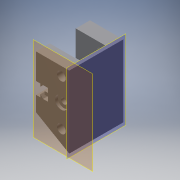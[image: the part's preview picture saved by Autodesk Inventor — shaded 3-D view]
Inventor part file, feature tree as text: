
AUTODESK INVENTOR PART (.ipt)
format: ipt  version: 2016 (Build 200138000, 138)  size: 259,584 bytes
history: native  units: in
note: dims shown in document units (in); Inventor stores cm internally (conversion verified against a paired STEP export)
features: sketch x10, extrude x10, projected_geometry x8, plane x4, reference x1
ambient origin geometry x8: Origin, YZ Plane, XZ Plane, XY Plane, X Axis, Y Axis, Z Axis, Center Point
bodies: Solid1 (feature_tree)
feature tree (33):
  plane  "Work Plane1"
  plane  "Work Plane2"
  sketch  "Sketch1"  dims[d0=60.0deg d1=1.0in d2=0.0in]
  plane  "Work Plane3"
  extrude  "Extrusion1"  Depth=1.0in TaperAngle=0.0deg
  extrude  "Extrusion2"  Depth=0.6299in
  extrude  "Extrusion3"  Depth=0.4331in
  extrude  "Extrusion4"  Depth=0.9055in
  sketch  "Sketch5"  dims[d11=0.1969in d12=0.0in d13=0.5in]
  plane  "Work Plane4"
  extrude  "Extrusion5"  Depth=0.5in
  extrude  "Extrusion6"  Depth=0.2756in TaperAngle=0.0deg
  extrude  "Extrusion7"  Depth=0.8661in
  extrude  "Extrusion8"  Depth=0.1181in
  extrude  "Extrusion9"  Depth=0.2362in
  extrude  "Extrusion10"  Depth=0.1969in
  reference  "Reference1"
  sketch  "Sketch2"  dims[d3=2.4375in d4=0.0in d5=0.6299in]
  sketch  "Sketch3"  dims[d6=0.6299in d7=0.4331in]
  projected_geometry  "Projected Loop1"
  sketch  "Sketch4"  dims[d8=8.9375in d9=0.0in d10=0.9055in]
  projected_geometry  "Projected Loop2"
  sketch  "Sketch6"  dims[d14=0.1969in d15=0.0in d16=0.2756in d17=0.0in]
  projected_geometry  "Projected Loop3"
  sketch  "Sketch7"  dims[d18=0.8661in d19=0.8661in]
  projected_geometry  "Projected Loop4"
  sketch  "Sketch8"  dims[d20=20.0in d21=0.0in d22=0.1181in]
  projected_geometry  "Projected Loop5"
  sketch  "Sketch10"  dims[d23=0.2362in d24=0.2362in]
  projected_geometry  "Projected Loop7"
  sketch  "Sketch11"  dims[d25=0.1181in d26=0.1969in d27=0.1969in d28=20.0in d29=0.0in d32=20.0in d33=0.0in d34=1.0in d35=1.0in d36=0.5in d37=0.25in d38=0.25in d39=1.0in d40=0.0in]
  projected_geometry  "Projected Loop8"
  projected_geometry  "Projected Loop9"
